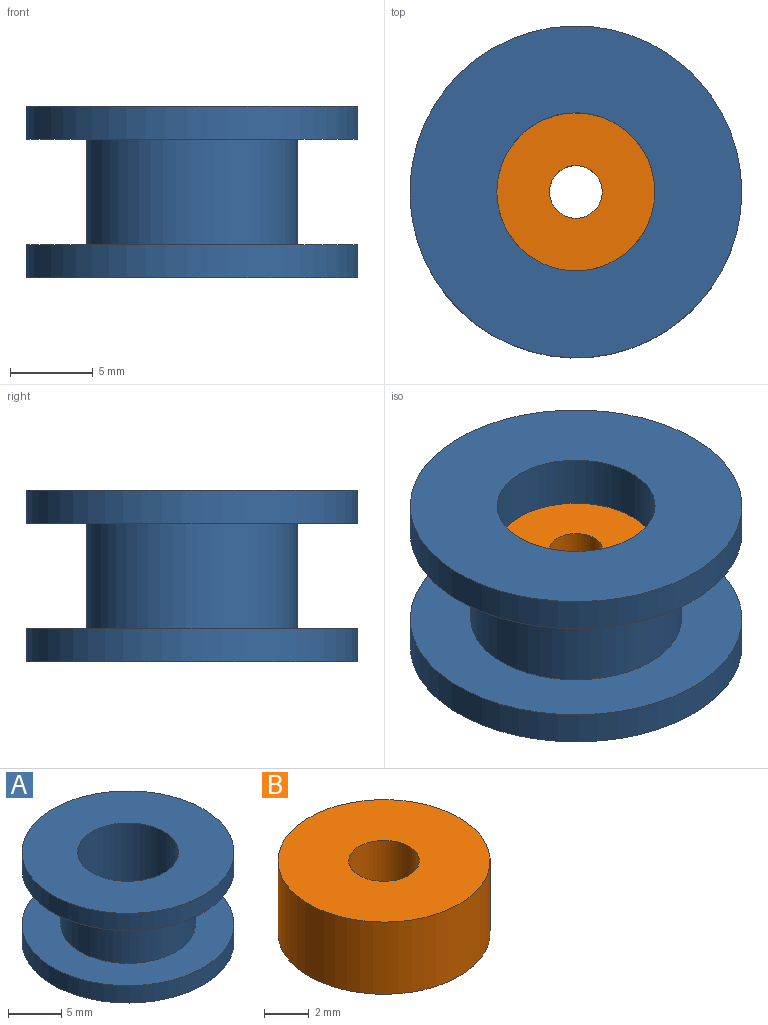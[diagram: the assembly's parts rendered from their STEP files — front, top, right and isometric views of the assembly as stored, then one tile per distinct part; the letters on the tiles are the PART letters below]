
ASSEMBLY  parts=2 mates=2
PART A: 8 faces, bbox 20x20x10.4 mm
  f0: cylinder r=10mm len=20mm, axis (0,0,-1), area 125.7mm2, adj f1,f2
  f1: plane 20x20mm, normal (0,0,1), area 187.5mm2, adj f0,f3
  f2: plane 20x20mm, normal (0,0,-1), area 242.9mm2, adj f0,f7
  f3: cylinder r=6.35mm len=12.7mm, axis (0,0,-1), area 253.4mm2, adj f1,f5
  f4: cylinder r=10mm len=20mm, axis (0,0,1), area 125.7mm2, adj f5,f6
  f5: plane 20x20mm, normal (0,0,-1), area 187.5mm2, adj f3,f4
  f6: plane 20x20mm, normal (0,0,1), area 242.9mm2, adj f4,f7
  f7: cylinder r=4.76mm len=10.35mm, axis (0,0,-1), area 309.7mm2, adj f2,f6
PART B: 4 faces, bbox 9.5x9.5x4 mm
  f0: cylinder r=1.59mm len=3.97mm, axis (0,0,-1), area 39.6mm2, adj f2,f3
  f1: cylinder r=4.76mm len=9.53mm, axis (0,0,-1), area 118.8mm2, adj f2,f3
  f2: plane 9.53x9.53mm, normal (0,0,1), area 63.3mm2, adj f0,f1
  f3: plane 9.53x9.53mm, normal (0,0,-1), area 63.3mm2, adj f0,f1
PLACE A t=(-0.67,-2.86,-8.9)mm
PLACE B t=(-0.67,-2.86,-5.69)mm
MATE slider A.f7 <-> B.f1  axis (0,0,-1) through (-0.67,-2.86,1.45)mm
MATE planar A.f3 <-> B.f1  axis (0,0,1) through (-0.67,-2.86,1.45)mm
